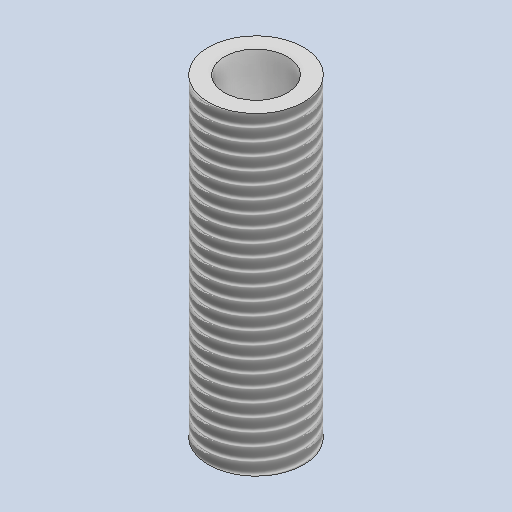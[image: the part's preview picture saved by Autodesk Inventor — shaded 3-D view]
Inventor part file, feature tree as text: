
AUTODESK INVENTOR PART (.ipt)
format: ipt  version: 2024 (Build 280153000, 153)  size: 157,696 bytes
history: native  units: mm
features: other x4, sketch x2
ambient origin geometry x8: Origin, YZ Plane, XZ Plane, XY Plane, X Axis, Y Axis, Z Axis, Center Point
bodies: Body1 (feature_tree)
feature tree (6):
  other  "TORNILLO_B.ipt"
  other  "Sólido1::TORNILLO_B.ipt"
  other  "OperaciónIdentificador1"
  sketch  "Boceto1"  dims[d0=10.0mm]
  sketch  "Boceto2"
  other  "Sólido1"
